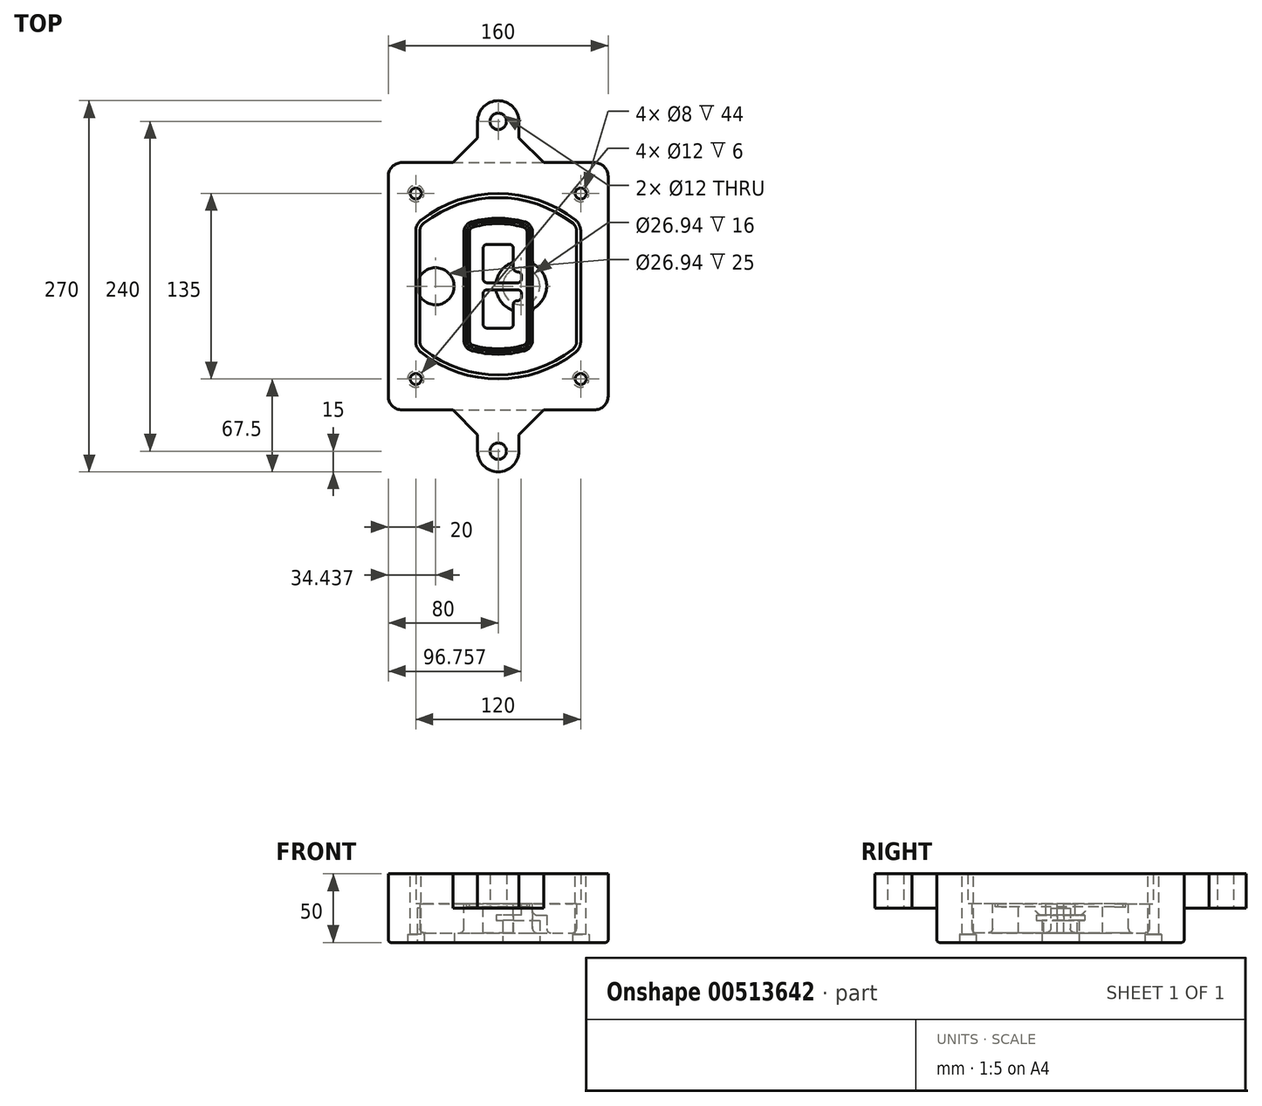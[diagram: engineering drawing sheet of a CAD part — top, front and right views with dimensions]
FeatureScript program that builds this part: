
annotation { "Feature Type Name" : "Feature", "Feature Type Description" : "" }
export const myFeature = defineFeature(function(context is Context, id is Id, definition is map)
    precondition{}
    {
        {
            var Q0;
            Q0=qCreatedBy(makeId("Top.planeOp"),FACE);
            var sketch = newSketch(context, id + "F0", { "sketchPlane" : qUnion([Q0])});
            skPoint(sketch, "E0.rect.middle", {"position": v(0, 0) * mm});
            skLineSegment(sketch, "E1.bottom", {"start": v(-70, -90) * mm, "end": v(70, -90) * mm});
            skLineSegment(sketch, "E1.top", {"start": v(-70, 90) * mm, "end": v(70, 90) * mm});
            skLineSegment(sketch, "E1.left", {"start": v(-80, -80) * mm, "end": v(-80, 80) * mm});
            skLineSegment(sketch, "E1.right", {"start": v(80, -80) * mm, "end": v(80, 80) * mm});
            skLineSegment(sketch, "E2", {"start": v(-80, 90) * mm, "end": v(80, -90) * mm, "construction": true});
            skLineSegment(sketch, "E3", {"start": v(80, 90) * mm, "end": v(-80, -90) * mm, "construction": true});
            skCircle(sketch, "E4", {"center": v(-60, 67.5) * mm, "radius": 4 * mm});
            skCircle(sketch, "E5", {"center": v(60, 67.5) * mm, "radius": 4 * mm});
            skCircle(sketch, "E6", {"center": v(60, -67.5) * mm, "radius": 4 * mm});
            skCircle(sketch, "E7", {"center": v(-60, -67.5) * mm, "radius": 4 * mm});
            skLineSegment(sketch, "E8", {"start": v(-60, 67.5) * mm, "end": v(60, 67.5) * mm, "construction": true});
            skLineSegment(sketch, "E9", {"start": v(60, 67.5) * mm, "end": v(60, -67.5) * mm, "construction": true});
            skLineSegment(sketch, "E10", {"start": v(60, -67.5) * mm, "end": v(-60, -67.5) * mm, "construction": true});
            skLineSegment(sketch, "E11", {"start": v(-60, -67.5) * mm, "end": v(-60, 67.5) * mm, "construction": true});
            skLineSegment(sketch, "E12", {"start": v(-60, 40.3) * mm, "end": v(-60, -40.3) * mm});
            skLineSegment(sketch, "E13", {"start": v(60, 40.3) * mm, "end": v(60, -40.3) * mm});
            skArc(sketch, "E14", {"start": v(56.15, 48.18) * mm, "mid": v(0, 67.5) * mm, "end": v(-56.15, 48.18) * mm});
            skArc(sketch, "E15", {"start": v(-56.15, -48.18) * mm, "mid": v(0, -67.5) * mm, "end": v(56.15, -48.18) * mm});
            skLineSegment(sketch, "E16", {"start": v(-60, 0) * mm, "end": v(60, 0) * mm, "construction": true});
            skPoint(sketch, "E17.visualSharp", {"position": v(-60, -45) * mm});
            skArc(sketch, "E17.filletArc", {"start": v(-60, -40.3) * mm, "mid": v(-58.99, -44.68) * mm, "end": v(-56.15, -48.18) * mm});
            skPoint(sketch, "E18.visualSharp", {"position": v(-60, 45) * mm});
            skArc(sketch, "E18.filletArc", {"start": v(-56.15, 48.18) * mm, "mid": v(-58.99, 44.68) * mm, "end": v(-60, 40.3) * mm});
            skPoint(sketch, "E19.visualSharp", {"position": v(60, 45) * mm});
            skArc(sketch, "E19.filletArc", {"start": v(60, 40.3) * mm, "mid": v(58.99, 44.68) * mm, "end": v(56.15, 48.18) * mm});
            skPoint(sketch, "E20.visualSharp", {"position": v(60, -45) * mm});
            skArc(sketch, "E20.filletArc", {"start": v(56.15, -48.18) * mm, "mid": v(58.99, -44.68) * mm, "end": v(60, -40.3) * mm});
            skPoint(sketch, "E21.visualSharp", {"position": v(-80, 90) * mm});
            skArc(sketch, "E21.filletArc", {"start": v(-70, 90) * mm, "mid": v(-77.07, 87.07) * mm, "end": v(-80, 80) * mm});
            skPoint(sketch, "E22.visualSharp", {"position": v(80, 90) * mm});
            skArc(sketch, "E22.filletArc", {"start": v(80, 80) * mm, "mid": v(77.07, 87.07) * mm, "end": v(70, 90) * mm});
            skPoint(sketch, "E23.visualSharp", {"position": v(80, -90) * mm});
            skArc(sketch, "E23.filletArc", {"start": v(70, -90) * mm, "mid": v(77.07, -87.07) * mm, "end": v(80, -80) * mm});
            skPoint(sketch, "E24.visualSharp", {"position": v(-80, -90) * mm});
            skArc(sketch, "E24.filletArc", {"start": v(-80, -80) * mm, "mid": v(-77.07, -87.07) * mm, "end": v(-70, -90) * mm});
            skArc(sketch, "E25.0", {"start": v(57, 40.3) * mm, "mid": v(56.3, 43.36) * mm, "end": v(54.3, 45.81) * mm});
            skLineSegment(sketch, "E25.1", {"start": v(57, 40.3) * mm, "end": v(57, -40.3) * mm});
            skArc(sketch, "E25.2", {"start": v(54.3, -45.81) * mm, "mid": v(56.3, -43.36) * mm, "end": v(57, -40.3) * mm});
            skArc(sketch, "E25.3", {"start": v(-54.3, -45.81) * mm, "mid": v(0, -64.5) * mm, "end": v(54.3, -45.81) * mm});
            skArc(sketch, "E25.4", {"start": v(-57, -40.3) * mm, "mid": v(-56.3, -43.36) * mm, "end": v(-54.3, -45.81) * mm});
            skArc(sketch, "E25.5", {"start": v(54.3, 45.81) * mm, "mid": v(0, 64.5) * mm, "end": v(-54.3, 45.81) * mm});
            skLineSegment(sketch, "E25.6", {"start": v(-57, 40.3) * mm, "end": v(-57, -40.3) * mm});
            skArc(sketch, "E25.7", {"start": v(-54.3, 45.81) * mm, "mid": v(-56.3, 43.36) * mm, "end": v(-57, 40.3) * mm});
            skArc(sketch, "E26.0", {"start": v(-58.62, 51.33) * mm, "mid": v(-62.58, 46.43) * mm, "end": v(-64, 40.3) * mm});
            skArc(sketch, "E26.1", {"start": v(58.62, 51.33) * mm, "mid": v(0, 71.5) * mm, "end": v(-58.62, 51.33) * mm});
            skArc(sketch, "E26.2", {"start": v(64, 40.3) * mm, "mid": v(62.58, 46.43) * mm, "end": v(58.62, 51.33) * mm});
            skLineSegment(sketch, "E26.3", {"start": v(64, 40.3) * mm, "end": v(64, -40.3) * mm});
            skArc(sketch, "E26.4", {"start": v(58.62, -51.33) * mm, "mid": v(62.58, -46.43) * mm, "end": v(64, -40.3) * mm});
            skLineSegment(sketch, "E26.5", {"start": v(-64, 40.3) * mm, "end": v(-64, -40.3) * mm});
            skArc(sketch, "E26.6", {"start": v(-58.62, -51.33) * mm, "mid": v(0, -71.5) * mm, "end": v(58.62, -51.33) * mm});
            skArc(sketch, "E26.7", {"start": v(-64, -40.3) * mm, "mid": v(-62.58, -46.43) * mm, "end": v(-58.62, -51.33) * mm});
            skSolve(sketch);
        }
        {
            var Q0;
            Q0=makeQuery(id+"F0.imprint","IMPRINT",FACE,{"disambiguationData":[TD([[makeQuery(id+"F0.imprint","IMPRINT",EDGE,{"derivedFrom":sQuery(id+"F0.wireOp",EDGE,"E1.bottom")}),1.0]])]});
            var Q1;
            Q1=makeQuery(id+"F0.imprint","IMPRINT",FACE,{"disambiguationData":[TD([[makeQuery(id+"F0.imprint","IMPRINT",EDGE,{"derivedFrom":sQuery(id+"F0.wireOp",EDGE,"E12")}),1.0]])]});
            var Q2;
            Q2=makeQuery(id+"F0.imprint","IMPRINT",FACE,{"disambiguationData":[TD([[makeQuery(id+"F0.imprint","IMPRINT",EDGE,{"derivedFrom":sQuery(id+"F0.wireOp",EDGE,"E25.0")}),1.0]])]});
            var Q3;
            Q3=makeQuery(id+"F0.imprint","IMPRINT",FACE,{"disambiguationData":[TD([[makeQuery(id+"F0.imprint","IMPRINT",EDGE,{"derivedFrom":sQuery(id+"F0.wireOp",EDGE,"E12")}),-1.0]])]});
            extrude(context, id + "F1", {"entities" : qUnion([Q0, Q1, Q2, Q3]), "oppositeDirection" : true, "depth" : 25 * mm});
        }
        {
            var Q0;
            Q0=makeQuery(id+"F0.imprint","IMPRINT",FACE,{"disambiguationData":[TD([[makeQuery(id+"F0.imprint","IMPRINT",EDGE,{"derivedFrom":sQuery(id+"F0.wireOp",EDGE,"E12")}),1.0]])]});
            extrude(context, id + "F2", {"entities" : qUnion([Q0]), "operationType" : NewBodyOperationType.ADD, "depth" : 3 * mm});
        }
        {
            var Q0;
            Q0=makeQuery(id+"F0.imprint","IMPRINT",FACE,{"disambiguationData":[TD([[makeQuery(id+"F0.imprint","IMPRINT",EDGE,{"derivedFrom":sQuery(id+"F0.wireOp",EDGE,"E25.0")}),1.0]])]});
            extrude(context, id + "F3", {"entities" : qUnion([Q0]), "operationType" : NewBodyOperationType.REMOVE, "oppositeDirection" : true, "depth" : 18 * mm});
        }
        {
            var Q0;
            Q0=makeQuery(id+"F2.opExtrude","CAP_FACE",FACE,{"disambiguationData":[OSD([sQuery(id+"F0.wireOp",EDGE,"E12"),sQuery(id+"F0.wireOp",EDGE,"E13"),sQuery(id+"F0.wireOp",EDGE,"E14"),sQuery(id+"F0.wireOp",EDGE,"E15"),sQuery(id+"F0.wireOp",EDGE,"E17.filletArc"),sQuery(id+"F0.wireOp",EDGE,"E18.filletArc"),sQuery(id+"F0.wireOp",EDGE,"E19.filletArc"),sQuery(id+"F0.wireOp",EDGE,"E20.filletArc"),sQuery(id+"F0.wireOp",EDGE,"E25.0"),sQuery(id+"F0.wireOp",EDGE,"E25.1"),sQuery(id+"F0.wireOp",EDGE,"E25.2"),sQuery(id+"F0.wireOp",EDGE,"E25.3"),sQuery(id+"F0.wireOp",EDGE,"E25.4"),sQuery(id+"F0.wireOp",EDGE,"E25.5"),sQuery(id+"F0.wireOp",EDGE,"E25.6"),sQuery(id+"F0.wireOp",EDGE,"E25.7")])],"isStart":false});
            var sketch = newSketch(context, id + "F4", { "sketchPlane" : qUnion([Q0])});
            skArc(sketch, "E27.0", {"start": v(-19.08, -46.97) * mm, "mid": v(0, -49.5) * mm, "end": v(19.08, -46.97) * mm});
            skArc(sketch, "E28.0", {"start": v(19.08, 46.97) * mm, "mid": v(0, 49.5) * mm, "end": v(-19.08, 46.97) * mm});
            skLineSegment(sketch, "E29", {"start": v(-25, 39.25) * mm, "end": v(-25, -39.25) * mm});
            skLineSegment(sketch, "E30", {"start": v(25, 39.25) * mm, "end": v(25, -39.25) * mm});
            skLineSegment(sketch, "E31", {"start": v(-25, 45.1) * mm, "end": v(25, 45.1) * mm, "construction": true});
            skLineSegment(sketch, "E32", {"start": v(-25, -45.1) * mm, "end": v(25, -45.1) * mm, "construction": true});
            skPoint(sketch, "E33.visualSharp", {"position": v(-25, 45.1) * mm});
            skArc(sketch, "E33.filletArc", {"start": v(-19.08, 46.97) * mm, "mid": v(-23.35, 44.11) * mm, "end": v(-25, 39.25) * mm});
            skPoint(sketch, "E34.visualSharp", {"position": v(25, 45.1) * mm});
            skArc(sketch, "E34.filletArc", {"start": v(25, 39.25) * mm, "mid": v(23.35, 44.11) * mm, "end": v(19.08, 46.97) * mm});
            skPoint(sketch, "E35.visualSharp", {"position": v(25, -45.1) * mm});
            skArc(sketch, "E35.filletArc", {"start": v(19.08, -46.97) * mm, "mid": v(23.35, -44.11) * mm, "end": v(25, -39.25) * mm});
            skPoint(sketch, "E36.visualSharp", {"position": v(-25, -45.1) * mm});
            skArc(sketch, "E36.filletArc", {"start": v(-25, -39.25) * mm, "mid": v(-23.35, -44.11) * mm, "end": v(-19.08, -46.97) * mm});
            skArc(sketch, "E37.0", {"start": v(54.3, 45.81) * mm, "mid": v(0, 64.5) * mm, "end": v(-54.3, 45.81) * mm});
            skArc(sketch, "E37.1", {"start": v(-54.3, 45.81) * mm, "mid": v(-56.3, 43.36) * mm, "end": v(-57, 40.3) * mm});
            skLineSegment(sketch, "E37.2", {"start": v(-57, 40.3) * mm, "end": v(-57, -40.3) * mm});
            skArc(sketch, "E37.3", {"start": v(-57, -40.3) * mm, "mid": v(-56.3, -43.36) * mm, "end": v(-54.3, -45.81) * mm});
            skArc(sketch, "E37.4", {"start": v(-54.3, -45.81) * mm, "mid": v(0, -64.5) * mm, "end": v(54.3, -45.81) * mm});
            skArc(sketch, "E37.5", {"start": v(54.3, -45.81) * mm, "mid": v(56.3, -43.36) * mm, "end": v(57, -40.3) * mm});
            skLineSegment(sketch, "E37.6", {"start": v(57, 40.3) * mm, "end": v(57, -40.3) * mm});
            skArc(sketch, "E37.7", {"start": v(57, 40.3) * mm, "mid": v(56.3, 43.36) * mm, "end": v(54.3, 45.81) * mm});
            skLineSegment(sketch, "E38.0", {"start": v(23, 39.25) * mm, "end": v(23, -39.25) * mm});
            skArc(sketch, "E38.1", {"start": v(18.56, -45.04) * mm, "mid": v(21.76, -42.9) * mm, "end": v(23, -39.25) * mm});
            skArc(sketch, "E38.2", {"start": v(-18.56, -45.04) * mm, "mid": v(0, -47.5) * mm, "end": v(18.56, -45.04) * mm});
            skArc(sketch, "E38.3", {"start": v(-23, -39.25) * mm, "mid": v(-21.76, -42.9) * mm, "end": v(-18.56, -45.04) * mm});
            skLineSegment(sketch, "E38.4", {"start": v(-23, 39.25) * mm, "end": v(-23, -39.25) * mm});
            skArc(sketch, "E38.5", {"start": v(23, 39.25) * mm, "mid": v(21.76, 42.9) * mm, "end": v(18.56, 45.04) * mm});
            skArc(sketch, "E38.6", {"start": v(-18.56, 45.04) * mm, "mid": v(-21.76, 42.9) * mm, "end": v(-23, 39.25) * mm});
            skArc(sketch, "E38.7", {"start": v(18.56, 45.04) * mm, "mid": v(0, 47.5) * mm, "end": v(-18.56, 45.04) * mm});
            skArc(sketch, "E39.0", {"start": v(21, 39.25) * mm, "mid": v(20.18, 41.68) * mm, "end": v(18.04, 43.1) * mm});
            skLineSegment(sketch, "E39.1", {"start": v(21, 39.25) * mm, "end": v(21, -39.25) * mm});
            skArc(sketch, "E39.2", {"start": v(18.04, -43.1) * mm, "mid": v(20.18, -41.68) * mm, "end": v(21, -39.25) * mm});
            skArc(sketch, "E39.3", {"start": v(-18.04, -43.1) * mm, "mid": v(0, -45.5) * mm, "end": v(18.04, -43.1) * mm});
            skArc(sketch, "E39.4", {"start": v(-21, -39.25) * mm, "mid": v(-20.18, -41.68) * mm, "end": v(-18.04, -43.1) * mm});
            skArc(sketch, "E39.5", {"start": v(18.04, 43.1) * mm, "mid": v(0, 45.5) * mm, "end": v(-18.04, 43.1) * mm});
            skLineSegment(sketch, "E39.6", {"start": v(-21, 39.25) * mm, "end": v(-21, -39.25) * mm});
            skArc(sketch, "E39.7", {"start": v(-18.04, 43.1) * mm, "mid": v(-20.18, 41.68) * mm, "end": v(-21, 39.25) * mm});
            skLineSegment(sketch, "E40", {"start": v(-25, 0) * mm, "end": v(25, 0) * mm, "construction": true});
            skLineSegment(sketch, "E41", {"start": v(-11, 5.5) * mm, "end": v(-11, 27.5) * mm});
            skLineSegment(sketch, "E42", {"start": v(-8, 30.5) * mm, "end": v(8, 30.5) * mm});
            skLineSegment(sketch, "E43", {"start": v(11, 27.5) * mm, "end": v(11, 13.5) * mm});
            skLineSegment(sketch, "E44", {"start": v(14, 10.5) * mm, "end": v(14, 10.5) * mm});
            skLineSegment(sketch, "E45", {"start": v(17, 7.5) * mm, "end": v(17, 5.5) * mm});
            skLineSegment(sketch, "E46", {"start": v(14, 2.5) * mm, "end": v(-8, 2.5) * mm});
            skPoint(sketch, "E47.visualSharp", {"position": v(-11, 30.5) * mm});
            skArc(sketch, "E47.filletArc", {"start": v(-8, 30.5) * mm, "mid": v(-10.12, 29.62) * mm, "end": v(-11, 27.5) * mm});
            skPoint(sketch, "E48.visualSharp", {"position": v(11, 30.5) * mm});
            skArc(sketch, "E48.filletArc", {"start": v(11, 27.5) * mm, "mid": v(10.12, 29.62) * mm, "end": v(8, 30.5) * mm});
            skPoint(sketch, "E49.visualSharp", {"position": v(11, 10.5) * mm});
            skArc(sketch, "E49.filletArc", {"start": v(11, 13.5) * mm, "mid": v(11.88, 11.38) * mm, "end": v(14, 10.5) * mm});
            skPoint(sketch, "E50.visualSharp", {"position": v(17, 10.5) * mm});
            skArc(sketch, "E50.filletArc", {"start": v(17, 7.5) * mm, "mid": v(16.12, 9.62) * mm, "end": v(14, 10.5) * mm});
            skPoint(sketch, "E51.visualSharp", {"position": v(17, 2.5) * mm});
            skArc(sketch, "E51.filletArc", {"start": v(14, 2.5) * mm, "mid": v(16.12, 3.38) * mm, "end": v(17, 5.5) * mm});
            skPoint(sketch, "E52.visualSharp", {"position": v(-11, 2.5) * mm});
            skArc(sketch, "E52.filletArc", {"start": v(-11, 5.5) * mm, "mid": v(-10.12, 3.38) * mm, "end": v(-8, 2.5) * mm});
            skLineSegment(sketch, "E53.0.MirrorCS", {"start": v(14, -2.5) * mm, "end": v(-8, -2.5) * mm});
            skArc(sketch, "E54.0.MirrorCS", {"start": v(-11, -5.5) * mm, "mid": v(-10.12, -3.38) * mm, "end": v(-8, -2.5) * mm});
            skLineSegment(sketch, "E55.0.MirrorCS", {"start": v(-11, -5.5) * mm, "end": v(-11, -27.5) * mm});
            skArc(sketch, "E56.0.MirrorCS", {"start": v(-8, -30.5) * mm, "mid": v(-10.12, -29.62) * mm, "end": v(-11, -27.5) * mm});
            skLineSegment(sketch, "E57.0.MirrorCS", {"start": v(-8, -30.5) * mm, "end": v(8, -30.5) * mm});
            skArc(sketch, "E58.0.MirrorCS", {"start": v(11, -27.5) * mm, "mid": v(10.12, -29.62) * mm, "end": v(8, -30.5) * mm});
            skLineSegment(sketch, "E59.0.MirrorCS", {"start": v(11, -27.5) * mm, "end": v(11, -13.5) * mm});
            skArc(sketch, "E60.0.MirrorCS", {"start": v(11, -13.5) * mm, "mid": v(11.88, -11.38) * mm, "end": v(14, -10.5) * mm});
            skArc(sketch, "E61.0.MirrorCS", {"start": v(17, -7.5) * mm, "mid": v(16.12, -9.62) * mm, "end": v(14, -10.5) * mm});
            skLineSegment(sketch, "E62.0.MirrorCS", {"start": v(17, -7.5) * mm, "end": v(17, -5.5) * mm});
            skArc(sketch, "E63.0.MirrorCS", {"start": v(14, -2.5) * mm, "mid": v(16.12, -3.38) * mm, "end": v(17, -5.5) * mm});
            skSolve(sketch);
        }
        {
            var Q0;
            Q0=makeQuery(id+"F4.imprint","IMPRINT",FACE,{"disambiguationData":[TD([[makeQuery(id+"F4.imprint","IMPRINT",EDGE,{"derivedFrom":sQuery(id+"F4.wireOp",EDGE,"E27.0")}),1.0]])]});
            var Q1;
            Q1=makeQuery(id+"F4.imprint","IMPRINT",FACE,{"disambiguationData":[TD([[makeQuery(id+"F4.imprint","IMPRINT",EDGE,{"derivedFrom":sQuery(id+"F4.wireOp",EDGE,"E38.0")}),-1.0]])]});
            var Q2;
            Q2=makeQuery(id+"F4.imprint","IMPRINT",FACE,{"disambiguationData":[TD([[makeQuery(id+"F4.imprint","IMPRINT",EDGE,{"derivedFrom":sQuery(id+"F4.wireOp",EDGE,"E39.0")}),1.0]])]});
            extrude(context, id + "F5", {"entities" : qUnion([Q0, Q1, Q2]), "operationType" : NewBodyOperationType.ADD, "endBound" : BoundingType.UP_TO_NEXT, "oppositeDirection" : true, "depth" : 25 * mm});
        }
        {
            var Q0;
            Q0=makeQuery(id+"F4.imprint","IMPRINT",FACE,{"disambiguationData":[TD([[makeQuery(id+"F4.imprint","IMPRINT",EDGE,{"derivedFrom":sQuery(id+"F4.wireOp",EDGE,"E38.0")}),-1.0]])]});
            extrude(context, id + "F6", {"entities" : qUnion([Q0]), "operationType" : NewBodyOperationType.REMOVE, "oppositeDirection" : true, "depth" : 2 * mm});
        }
        {
            var Q0;
            Q0=makeQuery(id+"F1.opExtrude","CAP_FACE",FACE,{"disambiguationData":[OSD([sQuery(id+"F0.wireOp",EDGE,"E1.bottom"),sQuery(id+"F0.wireOp",EDGE,"E1.top"),sQuery(id+"F0.wireOp",EDGE,"E1.left"),sQuery(id+"F0.wireOp",EDGE,"E1.right"),sQuery(id+"F0.wireOp",EDGE,"E4"),sQuery(id+"F0.wireOp",EDGE,"E5"),sQuery(id+"F0.wireOp",EDGE,"E6"),sQuery(id+"F0.wireOp",EDGE,"E7"),sQuery(id+"F0.wireOp",EDGE,"E21.filletArc"),sQuery(id+"F0.wireOp",EDGE,"E22.filletArc"),sQuery(id+"F0.wireOp",EDGE,"E23.filletArc"),sQuery(id+"F0.wireOp",EDGE,"E24.filletArc")])],"isStart":false});
            var sketch = newSketch(context, id + "F7", { "sketchPlane" : qUnion([Q0])});
            skCircle(sketch, "E64", {"center": v(16.76, 0) * mm, "radius": 13.47 * mm});
            skCircle(sketch, "E65", {"center": v(-45.56, 0) * mm, "radius": 13.47 * mm});
            skLineSegment(sketch, "E66", {"start": v(80, 0) * mm, "end": v(-80, 0) * mm});
            skCircle(sketch, "E67", {"center": v(16.76, 0) * mm, "radius": 18.47 * mm});
            skCircle(sketch, "E68", {"center": v(60, -67.5) * mm, "radius": 6 * mm});
            skCircle(sketch, "E69", {"center": v(-60, -67.5) * mm, "radius": 6 * mm});
            skCircle(sketch, "E70", {"center": v(-60, 67.5) * mm, "radius": 6 * mm});
            skCircle(sketch, "E71", {"center": v(60, 67.5) * mm, "radius": 6 * mm});
            skSolve(sketch);
        }
        {
            var Q0;
            {var subQ1=sQuery(id+"F7.wireOp",EDGE,"E66");var subQ4=sQuery(id+"F7.wireOp",EDGE,"E64");var subQ6=makeQuery(id+"F7.imprint","INTERSECT",VERTEX,{"disambiguationData":[OD(0.0)],"derivedFrom":[subQ4,subQ1]});Q0=makeQuery(id+"F7.imprint","IMPRINT",FACE,{"disambiguationData":[TD([[makeQuery(id+"F7.imprint","IMPRINT",EDGE,{"disambiguationData":[TD([[subQ6,-1.0]])],"derivedFrom":subQ4}),-1.0]])]});}
            var Q1;
            {var subQ0=sQuery(id+"F7.wireOp",EDGE,"E66");var subQ1=sQuery(id+"F7.wireOp",EDGE,"E64");var subQ3=makeQuery(id+"F7.imprint","INTERSECT",VERTEX,{"disambiguationData":[OD(0.0)],"derivedFrom":[subQ1,subQ0]});Q1=makeQuery(id+"F7.imprint","IMPRINT",FACE,{"disambiguationData":[TD([[makeQuery(id+"F7.imprint","IMPRINT",EDGE,{"disambiguationData":[TD([[subQ3,-1.0]])],"derivedFrom":subQ1}),1.0]])]});}
            var Q2;
            {var subQ0=sQuery(id+"F7.wireOp",EDGE,"E66");var subQ1=sQuery(id+"F7.wireOp",EDGE,"E64");var subQ3=makeQuery(id+"F7.imprint","INTERSECT",VERTEX,{"disambiguationData":[OD(0.0)],"derivedFrom":[subQ1,subQ0]});Q2=makeQuery(id+"F7.imprint","IMPRINT",FACE,{"disambiguationData":[TD([[makeQuery(id+"F7.imprint","IMPRINT",EDGE,{"disambiguationData":[TD([[subQ3,1.0]])],"derivedFrom":subQ1}),1.0]])]});}
            var Q3;
            {var subQ1=sQuery(id+"F7.wireOp",EDGE,"E66");var subQ4=sQuery(id+"F7.wireOp",EDGE,"E64");var subQ6=makeQuery(id+"F7.imprint","INTERSECT",VERTEX,{"disambiguationData":[OD(0.0)],"derivedFrom":[subQ4,subQ1]});Q3=makeQuery(id+"F7.imprint","IMPRINT",FACE,{"disambiguationData":[TD([[makeQuery(id+"F7.imprint","IMPRINT",EDGE,{"disambiguationData":[TD([[subQ6,1.0]])],"derivedFrom":subQ4}),-1.0]])]});}
            extrude(context, id + "F8", {"entities" : qUnion([Q0, Q1, Q2, Q3]), "operationType" : NewBodyOperationType.ADD, "oppositeDirection" : true, "depth" : 20 * mm});
        }
        {
            var Q0;
            {var subQ0=sQuery(id+"F7.wireOp",EDGE,"E66");var subQ1=sQuery(id+"F7.wireOp",EDGE,"E64");var subQ3=makeQuery(id+"F7.imprint","INTERSECT",VERTEX,{"disambiguationData":[OD(0.0)],"derivedFrom":[subQ1,subQ0]});Q0=makeQuery(id+"F7.imprint","IMPRINT",FACE,{"disambiguationData":[TD([[makeQuery(id+"F7.imprint","IMPRINT",EDGE,{"disambiguationData":[TD([[subQ3,-1.0]])],"derivedFrom":subQ1}),1.0]])]});}
            var Q1;
            {var subQ0=sQuery(id+"F7.wireOp",EDGE,"E66");var subQ1=sQuery(id+"F7.wireOp",EDGE,"E64");var subQ3=makeQuery(id+"F7.imprint","INTERSECT",VERTEX,{"disambiguationData":[OD(0.0)],"derivedFrom":[subQ1,subQ0]});Q1=makeQuery(id+"F7.imprint","IMPRINT",FACE,{"disambiguationData":[TD([[makeQuery(id+"F7.imprint","IMPRINT",EDGE,{"disambiguationData":[TD([[subQ3,1.0]])],"derivedFrom":subQ1}),1.0]])]});}
            extrude(context, id + "F9", {"entities" : qUnion([Q0, Q1]), "operationType" : NewBodyOperationType.REMOVE, "oppositeDirection" : true, "depth" : 16 * mm});
        }
        {
            var Q0;
            {var subQ0=sQuery(id+"F7.wireOp",EDGE,"E66");var subQ1=sQuery(id+"F7.wireOp",EDGE,"E65");var subQ3=makeQuery(id+"F7.imprint","INTERSECT",VERTEX,{"disambiguationData":[OD(0.0)],"derivedFrom":[subQ1,subQ0]});Q0=makeQuery(id+"F7.imprint","IMPRINT",FACE,{"disambiguationData":[TD([[makeQuery(id+"F7.imprint","IMPRINT",EDGE,{"disambiguationData":[TD([[subQ3,-1.0]])],"derivedFrom":subQ1}),1.0]])]});}
            var Q1;
            {var subQ0=sQuery(id+"F7.wireOp",EDGE,"E66");var subQ1=sQuery(id+"F7.wireOp",EDGE,"E65");var subQ3=makeQuery(id+"F7.imprint","INTERSECT",VERTEX,{"disambiguationData":[OD(0.0)],"derivedFrom":[subQ1,subQ0]});Q1=makeQuery(id+"F7.imprint","IMPRINT",FACE,{"disambiguationData":[TD([[makeQuery(id+"F7.imprint","IMPRINT",EDGE,{"disambiguationData":[TD([[subQ3,1.0]])],"derivedFrom":subQ1}),1.0]])]});}
            extrude(context, id + "F10", {"entities" : qUnion([Q0, Q1]), "operationType" : NewBodyOperationType.REMOVE, "oppositeDirection" : true, "depth" : 25 * mm});
        }
        {
            var Q0;
            Q0=makeQuery(id+"F7.imprint","IMPRINT",FACE,{"disambiguationData":[TD([[makeQuery(id+"F7.imprint","IMPRINT",EDGE,{"derivedFrom":sQuery(id+"F7.wireOp",EDGE,"E68")}),1.0]])]});
            var Q1;
            Q1=makeQuery(id+"F7.imprint","IMPRINT",FACE,{"disambiguationData":[TD([[makeQuery(id+"F7.imprint","IMPRINT",EDGE,{"derivedFrom":makeQuery(id+"F1.opExtrude","CAP_EDGE",EDGE,{"disambiguationData":[OSD([sQuery(id+"F0.wireOp",EDGE,"E5")])],"isStart":false})}),-1.0]])]});
            var Q2;
            Q2=makeQuery(id+"F7.imprint","IMPRINT",FACE,{"disambiguationData":[TD([[makeQuery(id+"F7.imprint","IMPRINT",EDGE,{"derivedFrom":sQuery(id+"F7.wireOp",EDGE,"E69")}),1.0]])]});
            var Q3;
            Q3=makeQuery(id+"F7.imprint","IMPRINT",FACE,{"disambiguationData":[TD([[makeQuery(id+"F7.imprint","IMPRINT",EDGE,{"derivedFrom":makeQuery(id+"F1.opExtrude","CAP_EDGE",EDGE,{"disambiguationData":[OSD([sQuery(id+"F0.wireOp",EDGE,"E4")])],"isStart":false})}),-1.0]])]});
            var Q4;
            Q4=makeQuery(id+"F7.imprint","IMPRINT",FACE,{"disambiguationData":[TD([[makeQuery(id+"F7.imprint","IMPRINT",EDGE,{"derivedFrom":sQuery(id+"F7.wireOp",EDGE,"E70")}),1.0]])]});
            var Q5;
            Q5=makeQuery(id+"F7.imprint","IMPRINT",FACE,{"disambiguationData":[TD([[makeQuery(id+"F7.imprint","IMPRINT",EDGE,{"derivedFrom":makeQuery(id+"F1.opExtrude","CAP_EDGE",EDGE,{"disambiguationData":[OSD([sQuery(id+"F0.wireOp",EDGE,"E7")])],"isStart":false})}),-1.0]])]});
            var Q6;
            Q6=makeQuery(id+"F7.imprint","IMPRINT",FACE,{"disambiguationData":[TD([[makeQuery(id+"F7.imprint","IMPRINT",EDGE,{"derivedFrom":sQuery(id+"F7.wireOp",EDGE,"E71")}),1.0]])]});
            var Q7;
            Q7=makeQuery(id+"F7.imprint","IMPRINT",FACE,{"disambiguationData":[TD([[makeQuery(id+"F7.imprint","IMPRINT",EDGE,{"derivedFrom":makeQuery(id+"F1.opExtrude","CAP_EDGE",EDGE,{"disambiguationData":[OSD([sQuery(id+"F0.wireOp",EDGE,"E6")])],"isStart":false})}),-1.0]])]});
            extrude(context, id + "F11", {"entities" : qUnion([Q0, Q1, Q2, Q3, Q4, Q5, Q6, Q7]), "operationType" : NewBodyOperationType.REMOVE, "oppositeDirection" : true, "depth" : 6 * mm});
        }
        {
            var Q0;
            Q0=makeQuery(id+"F9.boolean.opBoolean","COPY",FACE,{"derivedFrom":makeQuery(id+"F9.opExtrude","CAP_FACE",FACE,{"disambiguationData":[OSD([sQuery(id+"F7.wireOp",EDGE,"E64")])],"isStart":false})});
            var sketch = newSketch(context, id + "F12", { "sketchPlane" : qUnion([Q0])});
            skArc(sketch, "E72.0", {"start": v(11, 17.55) * mm, "mid": v(2.57, 11.82) * mm, "end": v(-1.54, 2.5) * mm});
            skArc(sketch, "E72.1", {"start": v(-1.54, -2.5) * mm, "mid": v(2.57, -11.82) * mm, "end": v(11, -17.55) * mm});
            skLineSegment(sketch, "E73", {"start": v(-1.54, -2.5) * mm, "end": v(14, -2.5) * mm});
            skLineSegment(sketch, "E74.0", {"start": v(14, 2.5) * mm, "end": v(-1.54, 2.5) * mm});
            skArc(sketch, "E74.1", {"start": v(14, 2.5) * mm, "mid": v(16.12, 3.38) * mm, "end": v(17, 5.5) * mm});
            skLineSegment(sketch, "E74.2", {"start": v(17, 7.5) * mm, "end": v(17, 5.5) * mm});
            skArc(sketch, "E74.3", {"start": v(17, 7.5) * mm, "mid": v(16.12, 9.62) * mm, "end": v(14, 10.5) * mm});
            skArc(sketch, "E74.4", {"start": v(11, 13.5) * mm, "mid": v(11.88, 11.38) * mm, "end": v(14, 10.5) * mm});
            skLineSegment(sketch, "E74.5", {"start": v(11, 17.55) * mm, "end": v(11, 13.5) * mm});
            skLineSegment(sketch, "E74.7", {"start": v(14, -2.5) * mm, "end": v(-1.54, -2.5) * mm});
            skArc(sketch, "E74.8", {"start": v(14, -2.5) * mm, "mid": v(16.12, -3.38) * mm, "end": v(17, -5.5) * mm});
            skLineSegment(sketch, "E74.9", {"start": v(17, -7.5) * mm, "end": v(17, -5.5) * mm});
            skArc(sketch, "E74.10", {"start": v(17, -7.5) * mm, "mid": v(16.12, -9.62) * mm, "end": v(14, -10.5) * mm});
            skArc(sketch, "E74.11", {"start": v(11, -13.5) * mm, "mid": v(11.88, -11.38) * mm, "end": v(14, -10.5) * mm});
            skLineSegment(sketch, "E74.12", {"start": v(11, -17.55) * mm, "end": v(11, -13.5) * mm});
            skPoint(sketch, "E75.orphan", {"position": v(11, -27.5) * mm});
            skPoint(sketch, "E76.orphan", {"position": v(-8, -2.5) * mm});
            skPoint(sketch, "E77.orphan", {"position": v(-8, 2.5) * mm});
            skPoint(sketch, "E78.orphan", {"position": v(11, 27.5) * mm});
            skSolve(sketch);
        }
        {
            var Q0;
            {var subQ7=sQuery(id+"F12.wireOp",EDGE,"E72.0");var subQ14=sQuery(id+"F12.wireOp",EDGE,"E72.1");var subQ16=sQuery(id+"F12.wireOp",EDGE,"E74.1");var subQ18=sQuery(id+"F12.wireOp",EDGE,"E74.8");Q0=qUnion([makeQuery(id+"F12.imprint","IMPRINT",FACE,{"disambiguationData":[TD([[makeQuery(id+"F12.imprint","IMPRINT",EDGE,{"derivedFrom":subQ7}),1.0]])]}),makeQuery(id+"F12.imprint","IMPRINT",FACE,{"disambiguationData":[TD([[makeQuery(id+"F12.imprint","IMPRINT",EDGE,{"derivedFrom":subQ14}),1.0]])]}),makeQuery(id+"F12.imprint","IMPRINT",FACE,{"disambiguationData":[TD([[makeQuery(id+"F12.imprint","IMPRINT",EDGE,{"derivedFrom":subQ16}),1.0]])]}),makeQuery(id+"F12.imprint","IMPRINT",FACE,{"disambiguationData":[TD([[makeQuery(id+"F12.imprint","IMPRINT",EDGE,{"derivedFrom":subQ18}),-1.0]])]})]);}
            var Q1;
            Q1=makeQuery(id+"F5.boolean.opBoolean","SPLIT",FACE,{"disambiguationData":[TD([makeQuery(id+"F5.opExtrude","SWEPT_FACE",FACE,{"disambiguationData":[OSD([sQuery(id+"F4.wireOp",EDGE,"E41")])]})])],"derivedFrom":makeQuery(id+"F3.boolean.opBoolean","COPY",FACE,{"derivedFrom":makeQuery(id+"F3.opExtrude","CAP_FACE",FACE,{"disambiguationData":[OSD([sQuery(id+"F0.wireOp",EDGE,"E25.0"),sQuery(id+"F0.wireOp",EDGE,"E25.1"),sQuery(id+"F0.wireOp",EDGE,"E25.2"),sQuery(id+"F0.wireOp",EDGE,"E25.3"),sQuery(id+"F0.wireOp",EDGE,"E25.4"),sQuery(id+"F0.wireOp",EDGE,"E25.5"),sQuery(id+"F0.wireOp",EDGE,"E25.6"),sQuery(id+"F0.wireOp",EDGE,"E25.7")])],"isStart":false})})});
            extrude(context, id + "F13", {"entities" : qUnion([Q0]), "operationType" : NewBodyOperationType.REMOVE, "endBound" : BoundingType.UP_TO_SURFACE, "endBoundEntityFace" : qUnion([Q1]), "depth" : 25 * mm});
        }
        {
            var Q0;
            Q0=makeQuery(id+"F3.boolean.opBoolean","COPY",EDGE,{"derivedFrom":makeQuery(id+"F3.opExtrude","CAP_EDGE",EDGE,{"disambiguationData":[OSD([sQuery(id+"F0.wireOp",EDGE,"E25.6")])],"isStart":false})});
            var Q1;
            Q1=makeQuery(id+"F8.boolean.opBoolean","INTERSECT",EDGE,{"derivedFrom":[makeQuery(id+"F5.opExtrude","SWEPT_FACE",FACE,{"disambiguationData":[OSD([sQuery(id+"F4.wireOp",EDGE,"E30")])]}),makeQuery(id+"F8.opExtrude","CAP_FACE",FACE,{"disambiguationData":[OSD([sQuery(id+"F7.wireOp",EDGE,"E67")])],"isStart":false})]});
            var Q2;
            Q2=makeQuery(id+"F8.boolean.opBoolean","INTERSECT",EDGE,{"disambiguationData":[OD(1.0)],"derivedFrom":[makeQuery(id+"F5.opExtrude","SWEPT_FACE",FACE,{"disambiguationData":[OSD([sQuery(id+"F4.wireOp",EDGE,"E30")])]}),makeQuery(id+"F8.opExtrude","SWEPT_FACE",FACE,{"disambiguationData":[OSD([sQuery(id+"F7.wireOp",EDGE,"E67")])]})]});
            var Q3;
            {var subQ0=sQuery(id+"F4.wireOp",EDGE,"E30");Q3=makeQuery(id+"F8.boolean.opBoolean","SPLIT",EDGE,{"disambiguationData":[TD([makeQuery(id+"F5.opExtrude","SWEPT_FACE",FACE,{"disambiguationData":[OSD([sQuery(id+"F4.wireOp",EDGE,"E35.filletArc")])]})])],"derivedFrom":makeQuery(id+"F5.opExtrude","CAP_EDGE",EDGE,{"disambiguationData":[OSD([subQ0])],"isStart":false})});}
            var Q4;
            {var subQ0=sQuery(id+"F0.wireOp",EDGE,"E25.7");var subQ1=sQuery(id+"F0.wireOp",EDGE,"E25.1");var subQ2=sQuery(id+"F0.wireOp",EDGE,"E25.6");var subQ3=sQuery(id+"F0.wireOp",EDGE,"E25.5");var subQ4=sQuery(id+"F0.wireOp",EDGE,"E25.4");var subQ5=sQuery(id+"F0.wireOp",EDGE,"E25.0");var subQ6=sQuery(id+"F0.wireOp",EDGE,"E25.2");var subQ7=sQuery(id+"F0.wireOp",EDGE,"E25.3");Q4=makeQuery(id+"F8.boolean.opBoolean","INTERSECT",EDGE,{"derivedFrom":[makeQuery(id+"F5.boolean.opBoolean","SPLIT",FACE,{"disambiguationData":[TD([makeQuery(id+"F2.opExtrude","SWEPT_FACE",FACE,{"disambiguationData":[OSD([subQ5])]})])],"derivedFrom":makeQuery(id+"F3.boolean.opBoolean","COPY",FACE,{"derivedFrom":makeQuery(id+"F3.opExtrude","CAP_FACE",FACE,{"disambiguationData":[OSD([subQ5,subQ1,subQ6,subQ7,subQ4,subQ3,subQ2,subQ0])],"isStart":false})})}),makeQuery(id+"F8.opExtrude","SWEPT_FACE",FACE,{"disambiguationData":[OSD([sQuery(id+"F7.wireOp",EDGE,"E67")])]})]});}
            var Q5;
            Q5=makeQuery(id+"F8.boolean.opBoolean","INTERSECT",EDGE,{"disambiguationData":[OD(0.0)],"derivedFrom":[makeQuery(id+"F5.opExtrude","SWEPT_FACE",FACE,{"disambiguationData":[OSD([sQuery(id+"F4.wireOp",EDGE,"E30")])]}),makeQuery(id+"F8.opExtrude","SWEPT_FACE",FACE,{"disambiguationData":[OSD([sQuery(id+"F7.wireOp",EDGE,"E67")])]})]});
            fillet(context, id + "F14", {"entities" : qUnion([Q0, Q1, Q2, Q3, Q4, Q5]), "radius" : 3 * mm, "tangentPropagation" : true, "allowEdgeOverflow" : false});
        }
        {
            var Q0;
            Q0=makeQuery(id+"F1.opExtrude","CAP_EDGE",EDGE,{"disambiguationData":[OSD([sQuery(id+"F0.wireOp",EDGE,"E1.bottom")])],"isStart":false});
            fillet(context, id + "F15", {"entities" : qUnion([Q0]), "radius" : 2 * mm, "tangentPropagation" : true, "allowEdgeOverflow" : false});
        }
        {
            var Q0;
            {var subQ0=sQuery(id+"F0.wireOp",EDGE,"E21.filletArc");var subQ1=sQuery(id+"F0.wireOp",EDGE,"E7");var subQ2=sQuery(id+"F0.wireOp",EDGE,"E6");var subQ3=sQuery(id+"F0.wireOp",EDGE,"E5");var subQ4=sQuery(id+"F0.wireOp",EDGE,"E4");var subQ5=sQuery(id+"F0.wireOp",EDGE,"E22.filletArc");var subQ6=sQuery(id+"F0.wireOp",EDGE,"E1.bottom");var subQ7=sQuery(id+"F0.wireOp",EDGE,"E1.right");var subQ8=sQuery(id+"F0.wireOp",EDGE,"E1.top");var subQ9=sQuery(id+"F0.wireOp",EDGE,"E1.left");var subQ10=sQuery(id+"F0.wireOp",EDGE,"E23.filletArc");var subQ11=sQuery(id+"F0.wireOp",EDGE,"E24.filletArc");Q0=makeQuery(id+"F2.boolean.opBoolean","SPLIT",FACE,{"disambiguationData":[TD([makeQuery(id+"F1.opExtrude","SWEPT_FACE",FACE,{"disambiguationData":[OSD([subQ6])]})])],"derivedFrom":makeQuery(id+"F1.opExtrude","CAP_FACE",FACE,{"disambiguationData":[OSD([subQ6,subQ8,subQ9,subQ7,subQ4,subQ3,subQ2,subQ1,subQ0,subQ5,subQ10,subQ11])],"isStart":true})});}
            var sketch = newSketch(context, id + "F16", { "sketchPlane" : qUnion([Q0])});
            skLineSegment(sketch, "E79.0", {"start": v(-80, -80) * mm, "end": v(-80, 80) * mm});
            skArc(sketch, "E79.1", {"start": v(-70, 90) * mm, "mid": v(-77.07, 87.07) * mm, "end": v(-80, 80) * mm});
            skLineSegment(sketch, "E79.2", {"start": v(-70, 90) * mm, "end": v(70, 90) * mm});
            skArc(sketch, "E79.3", {"start": v(80, 80) * mm, "mid": v(77.07, 87.07) * mm, "end": v(70, 90) * mm});
            skLineSegment(sketch, "E79.4", {"start": v(80, -80) * mm, "end": v(80, 80) * mm});
            skArc(sketch, "E79.5", {"start": v(70, -90) * mm, "mid": v(77.07, -87.07) * mm, "end": v(80, -80) * mm});
            skLineSegment(sketch, "E79.6", {"start": v(-70, -90) * mm, "end": v(70, -90) * mm});
            skArc(sketch, "E79.7", {"start": v(-80, -80) * mm, "mid": v(-77.07, -87.07) * mm, "end": v(-70, -90) * mm});
            skArc(sketch, "E79.8", {"start": v(-56.15, -48.18) * mm, "mid": v(0, -67.5) * mm, "end": v(56.15, -48.18) * mm});
            skLineSegment(sketch, "E79.9", {"start": v(-60, 40.3) * mm, "end": v(-60, -40.3) * mm});
            skArc(sketch, "E79.10", {"start": v(-60, -40.3) * mm, "mid": v(-58.99, -44.68) * mm, "end": v(-56.15, -48.18) * mm});
            skArc(sketch, "E79.11", {"start": v(56.15, -48.18) * mm, "mid": v(58.99, -44.68) * mm, "end": v(60, -40.3) * mm});
            skLineSegment(sketch, "E79.12", {"start": v(60, 40.3) * mm, "end": v(60, -40.3) * mm});
            skArc(sketch, "E79.13", {"start": v(60, 40.3) * mm, "mid": v(58.99, 44.68) * mm, "end": v(56.15, 48.18) * mm});
            skArc(sketch, "E79.14", {"start": v(56.15, 48.18) * mm, "mid": v(0, 67.5) * mm, "end": v(-56.15, 48.18) * mm});
            skArc(sketch, "E79.15", {"start": v(-56.15, 48.18) * mm, "mid": v(-58.99, 44.68) * mm, "end": v(-60, 40.3) * mm});
            skLineSegment(sketch, "E80", {"start": v(0, 90) * mm, "end": v(0, 120) * mm, "construction": true});
            skPoint(sketch, "E80.endSnap0", {"position": v(0, 90) * mm});
            skLineSegment(sketch, "E81", {"start": v(-33, 90) * mm, "end": v(-15, 108) * mm});
            skLineSegment(sketch, "E82", {"start": v(-15, 108) * mm, "end": v(-15, 120) * mm});
            skArc(sketch, "E83", {"start": v(-15, 120) * mm, "mid": v(0, 135) * mm, "end": v(15, 120) * mm});
            skCircle(sketch, "E84", {"center": v(0, 120) * mm, "radius": 6 * mm});
            skLineSegment(sketch, "E85", {"start": v(15, 120) * mm, "end": v(15, 108) * mm});
            skLineSegment(sketch, "E86", {"start": v(15, 108) * mm, "end": v(33, 90) * mm});
            skLineSegment(sketch, "E87", {"start": v(80, 0) * mm, "end": v(-80, 0) * mm, "construction": true});
            skLineSegment(sketch, "E88.MirrorCS", {"start": v(-33, -90) * mm, "end": v(-15, -108) * mm});
            skLineSegment(sketch, "E89.MirrorCS", {"start": v(-15, -108) * mm, "end": v(-15, -120) * mm});
            skArc(sketch, "E90.MirrorCS", {"start": v(-15, -120) * mm, "mid": v(0, -135) * mm, "end": v(15, -120) * mm});
            skCircle(sketch, "E91.MirrorC", {"center": v(0, -120) * mm, "radius": 6 * mm});
            skLineSegment(sketch, "E92.MirrorCS", {"start": v(15, -108) * mm, "end": v(33, -90) * mm});
            skLineSegment(sketch, "E93.MirrorCS", {"start": v(15, -120) * mm, "end": v(15, -108) * mm});
            skSolve(sketch);
        }
        {
            var Q0;
            {var subQ0=sQuery(id+"F16.wireOp",EDGE,"E81");Q0=makeQuery(id+"F16.imprint","IMPRINT",FACE,{"disambiguationData":[TD([[makeQuery(id+"F16.imprint","IMPRINT",EDGE,{"derivedFrom":subQ0}),-1.0]])]});}
            var Q1;
            Q1=makeQuery(id+"F16.imprint","IMPRINT",FACE,{"disambiguationData":[TD([[makeQuery(id+"F16.imprint","IMPRINT",EDGE,{"derivedFrom":sQuery(id+"F16.wireOp",EDGE,"E79.0")}),-1.0]])]});
            var Q2;
            {var subQ0=sQuery(id+"F16.wireOp",EDGE,"E88.MirrorCS");Q2=makeQuery(id+"F16.imprint","IMPRINT",FACE,{"disambiguationData":[TD([[makeQuery(id+"F16.imprint","IMPRINT",EDGE,{"derivedFrom":subQ0}),1.0]])]});}
            extrude(context, id + "F17", {"entities" : qUnion([Q0, Q1, Q2]), "operationType" : NewBodyOperationType.ADD, "depth" : 25 * mm});
        }
    });
